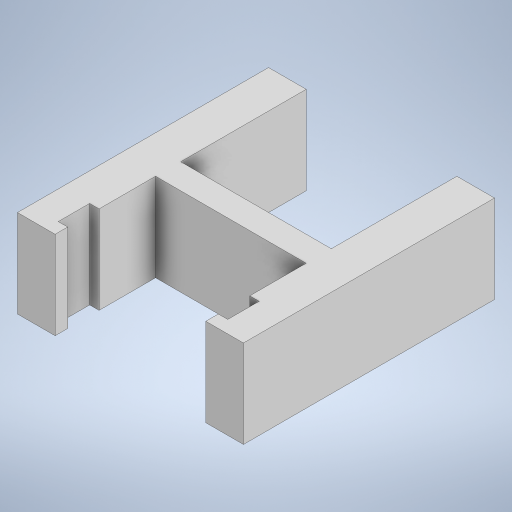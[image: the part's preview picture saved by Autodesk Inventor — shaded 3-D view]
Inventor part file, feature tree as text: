
AUTODESK INVENTOR PART (.ipt)
format: ipt  version: 2024 (Build 280153000, 153)  size: 234,496 bytes
history: native  units: in
note: dims shown in document units (in); Inventor stores cm internally (conversion verified against a paired STEP export)
features: extrude x1, sketch x1
ambient origin geometry x8: Origin, YZ Plane, XZ Plane, XY Plane, X Axis, Y Axis, Z Axis, Center Point
bodies: Solid1 (feature_tree)
feature tree (2):
  extrude  "Extrusion1"  Depth=0.1181in
  sketch  "Sketch1"  dims[d0=0.0984in d1=0.1181in d2=0.1181in d3=0.3937in d4=0.3937in d5=0.0787in d6=0.1181in d8=0.0394in d9=0.315in d10=0.7087in d11=0.0295in d12=0.0295in d13=0.1181in d14=0.2756in d15=0.0in]
